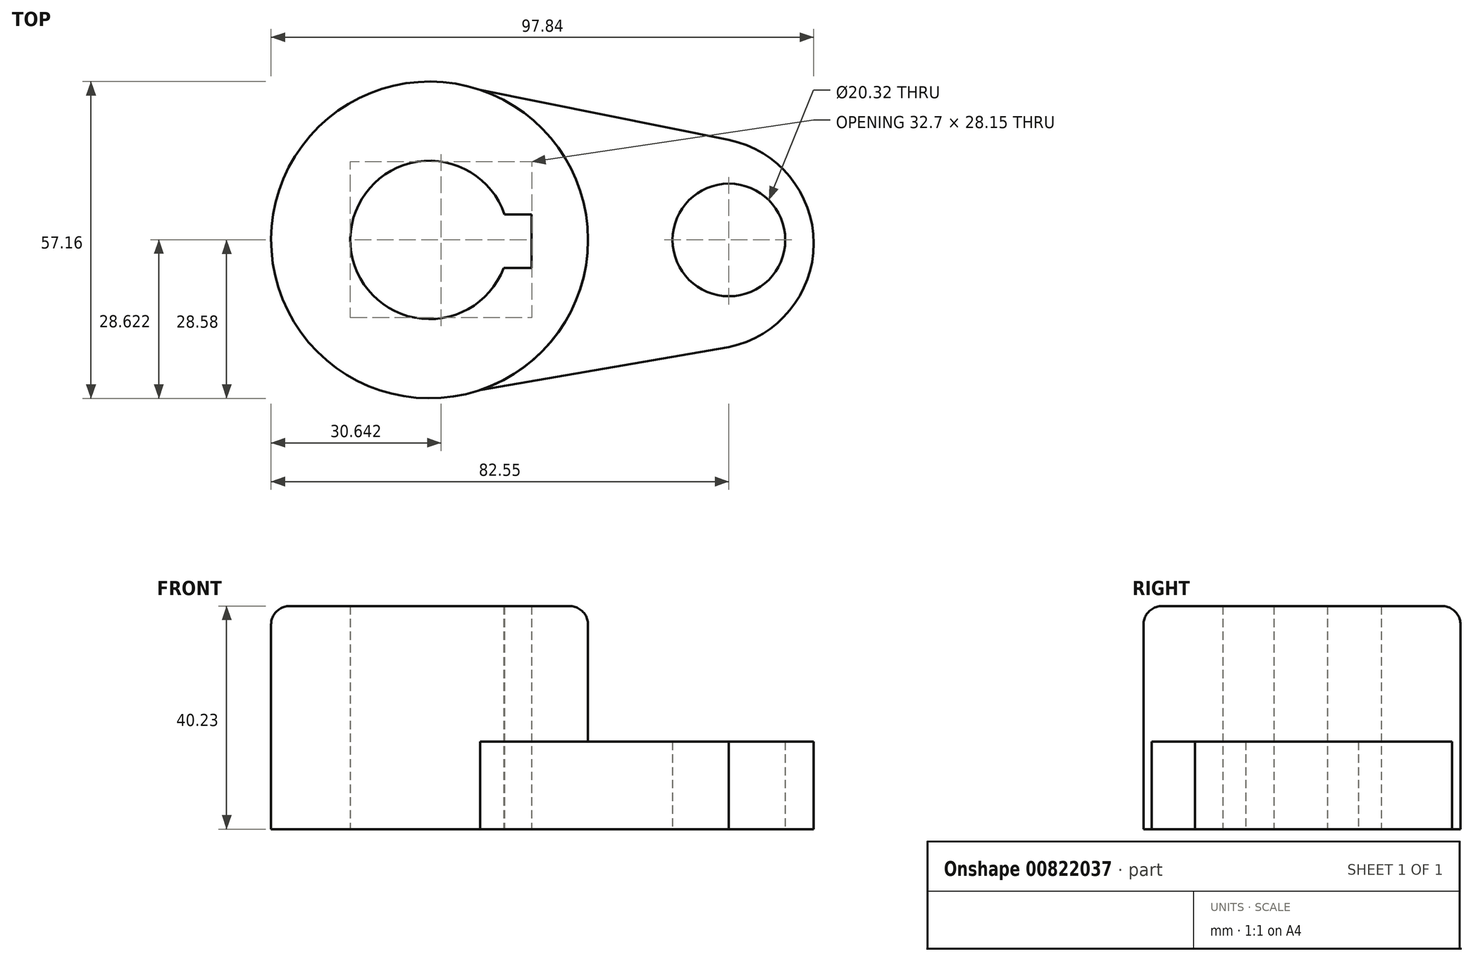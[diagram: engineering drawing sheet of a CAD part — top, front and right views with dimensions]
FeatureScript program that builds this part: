
annotation { "Feature Type Name" : "Feature", "Feature Type Description" : "" }
export const myFeature = defineFeature(function(context is Context, id is Id, definition is map)
    precondition{}
    {
        {
            var Q0;
            Q0=qCreatedBy(makeId("Top.planeOp"),FACE);
            var sketch = newSketch(context, id + "F0", { "sketchPlane" : qUnion([Q0])});
            skCircle(sketch, "E0", {"center": v(-53.98, 0) * mm, "radius": 28.58 * mm});
            skCircle(sketch, "E1", {"center": v(0, 0) * mm, "radius": 10.16 * mm});
            skCircle(sketch, "E2", {"center": v(-53.98, 0) * mm, "radius": 14.29 * mm});
            skLineSegment(sketch, "E3", {"start": v(-44.85, -27.08) * mm, "end": v(0, -19.3) * mm});
            skLineSegment(sketch, "E4", {"start": v(-40.45, 4.6) * mm, "end": v(-35.56, 4.6) * mm});
            skLineSegment(sketch, "E5", {"start": v(-35.56, 4.6) * mm, "end": v(-35.56, -5.05) * mm});
            skLineSegment(sketch, "E6", {"start": v(-35.56, -5.05) * mm, "end": v(-40.61, -5.05) * mm});
            skLineSegment(sketch, "E7", {"start": v(-44.85, 27.08) * mm, "end": v(0, 18.04) * mm});
            skArc(sketch, "E8", {"start": v(0, -19.3) * mm, "mid": v(15.29, -0.63) * mm, "end": v(0, 18.04) * mm});
            skSolve(sketch);
        }
        {
            var Q0;
            {var subQ0=sQuery(id+"F0.wireOp",EDGE,"E4");Q0=makeQuery(id+"F0.imprint","IMPRINT",FACE,{"disambiguationData":[TD([[makeQuery(id+"F0.imprint","IMPRINT",EDGE,{"derivedFrom":subQ0}),1.0]])]});}
            extrude(context, id + "F1", {"entities" : qUnion([Q0]), "depth" : 40.23 * mm, "offsetDistance" : 25.4 * mm});
        }
        {
            var Q0;
            Q0=makeQuery(id+"F0.imprint","IMPRINT",FACE,{"disambiguationData":[TD([[makeQuery(id+"F0.imprint","IMPRINT",EDGE,{"derivedFrom":sQuery(id+"F0.wireOp",EDGE,"E1")}),-1.0]])]});
            extrude(context, id + "F2", {"entities" : qUnion([Q0]), "operationType" : NewBodyOperationType.ADD, "depth" : 15.77 * mm, "offsetDistance" : 25.4 * mm});
        }
        {
            var Q0;
            Q0=makeQuery(id+"F1.opExtrude","CAP_EDGE",EDGE,{"disambiguationData":[OSD([sQuery(id+"F0.wireOp",EDGE,"E0")])],"isStart":false});
            fillet(context, id + "F3", {"entities" : qUnion([Q0]), "radius" : 3.3 * mm, "tangentPropagation" : true, "allowEdgeOverflow" : false});
        }
    });
